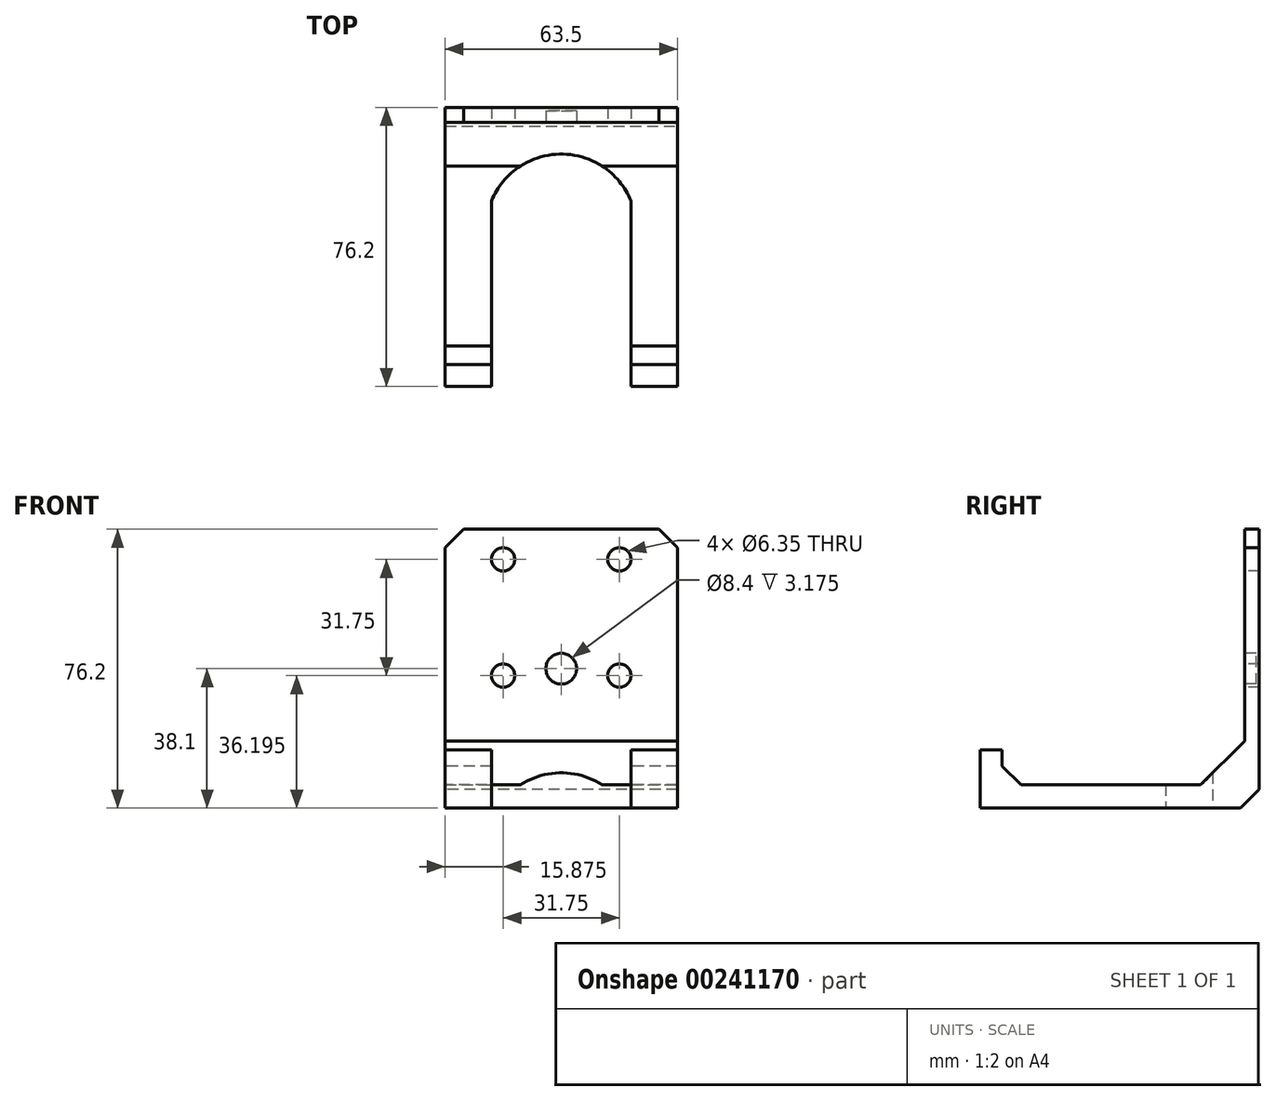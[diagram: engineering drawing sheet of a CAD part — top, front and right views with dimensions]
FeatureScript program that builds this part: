
annotation { "Feature Type Name" : "Feature", "Feature Type Description" : "" }
export const myFeature = defineFeature(function(context is Context, id is Id, definition is map)
    precondition{}
    {
        {
            var Q0;
            Q0=qCreatedBy(makeId("Right.planeOp"),FACE);
            var sketch = newSketch(context, id + "F0", { "sketchPlane" : qUnion([Q0])});
            skLineSegment(sketch, "E0", {"start": v(-72.2, 0) * mm, "end": v(-72.2, 15.87) * mm});
            skLineSegment(sketch, "E1", {"start": v(-72.2, 15.87) * mm, "end": v(-66.2, 15.87) * mm});
            skLineSegment(sketch, "E2", {"start": v(-66.2, 15.87) * mm, "end": v(-66.2, 6.35) * mm});
            skLineSegment(sketch, "E3", {"start": v(-66.2, 6.35) * mm, "end": v(0, 6.35) * mm});
            skLineSegment(sketch, "E4", {"start": v(0, 6.35) * mm, "end": v(0, 76.2) * mm});
            skLineSegment(sketch, "E5", {"start": v(0, 76.2) * mm, "end": v(4, 76.2) * mm});
            skLineSegment(sketch, "E6", {"start": v(4, 76.2) * mm, "end": v(4, 0) * mm});
            skLineSegment(sketch, "E7", {"start": v(4, 0) * mm, "end": v(-72.2, 0) * mm});
            skSolve(sketch);
        }
        {
            var Q0;
            Q0 = qSketchRegion(id + "F0", true);
            extrude(context, id + "F1", {"entities" : qUnion([Q0]), "flatOperationType" : FlatOperationType.REMOVE, "endBound" : BoundingType.SYMMETRIC, "offsetDistance" : 25.4 * mm, "depth" : 63.5 * mm, "domain" : OperationDomain.MODEL});
        }
        {
            var Q0;
            Q0=makeQuery(id+"F1.opExtrude","SWEPT_EDGE",EDGE,{"disambiguationData":[OSD([sQuery(id+"F0.wireOp",EDGE,"E3"),sQuery(id+"F0.wireOp",EDGE,"E4")])]});
            chamfer(context, id + "F2", {"entities" : qUnion([Q0]), "width" : 12 * mm, "tangentPropagation" : true});
        }
        {
            var Q0;
            Q0=qCreatedBy(makeId("Top.planeOp"),FACE);
            var sketch = newSketch(context, id + "F3", { "sketchPlane" : qUnion([Q0])});
            skLineSegment(sketch, "E8", {"start": v(-19.05, -72.2) * mm, "end": v(19.05, -72.2) * mm});
            skLineSegment(sketch, "E9", {"start": v(19.05, -72.2) * mm, "end": v(19.05, -21.52) * mm});
            skLineSegment(sketch, "E10", {"start": v(-19.05, -72.2) * mm, "end": v(-19.05, -21.52) * mm});
            skArc(sketch, "E11", {"start": v(19.05, -21.52) * mm, "mid": v(0, -8.7) * mm, "end": v(-19.05, -21.52) * mm});
            skSolve(sketch);
        }
        {
            var Q0;
            Q0 = qSketchRegion(id + "F3", true);
            extrude(context, id + "F4", {"entities" : qUnion([Q0]), "operationType" : NewBodyOperationType.REMOVE, "depth" : 25.4 * mm});
        }
        {
            var Q0;
            Q0=makeQuery(id+"F1.opExtrude","SWEPT_FACE",FACE,{"disambiguationData":[OSD([sQuery(id+"F0.wireOp",EDGE,"E4")])]});
            var sketch = newSketch(context, id + "F5", { "sketchPlane" : qUnion([Q0])});
            skCircle(sketch, "E12", {"center": v(-15.88, 67.95) * mm, "radius": 3.18 * mm});
            skCircle(sketch, "E13", {"center": v(15.88, 67.95) * mm, "radius": 3.18 * mm});
            skCircle(sketch, "E14", {"center": v(-15.87, 36.2) * mm, "radius": 3.18 * mm});
            skCircle(sketch, "E15", {"center": v(15.88, 36.2) * mm, "radius": 3.18 * mm});
            skSolve(sketch);
        }
        {
            var Q0;
            Q0 = qSketchRegion(id + "F5", true);
            extrude(context, id + "F6", {"entities" : qUnion([Q0]), "operationType" : NewBodyOperationType.REMOVE, "oppositeDirection" : true, "depth" : 25.4 * mm});
        }
        {
            var Q0;
            {var subQ0=sQuery(id+"F0.wireOp",EDGE,"E3");var subQ1=sQuery(id+"F0.wireOp",EDGE,"E2");Q0=makeQuery(id+"F4.boolean.opBoolean","SPLIT",EDGE,{"disambiguationData":[TD([makeQuery(id+"F4.opExtrude","SWEPT_FACE",FACE,{"disambiguationData":[OSD([sQuery(id+"F3.wireOp",EDGE,"E9")])]})])],"derivedFrom":makeQuery(id+"F1.opExtrude","SWEPT_EDGE",EDGE,{"disambiguationData":[OSD([subQ1,subQ0])]})});}
            var Q1;
            {var subQ0=sQuery(id+"F0.wireOp",EDGE,"E3");var subQ1=sQuery(id+"F0.wireOp",EDGE,"E2");Q1=makeQuery(id+"F4.boolean.opBoolean","SPLIT",EDGE,{"disambiguationData":[TD([makeQuery(id+"F4.opExtrude","SWEPT_FACE",FACE,{"disambiguationData":[OSD([sQuery(id+"F3.wireOp",EDGE,"E10")])]})])],"derivedFrom":makeQuery(id+"F1.opExtrude","SWEPT_EDGE",EDGE,{"disambiguationData":[OSD([subQ1,subQ0])]})});}
            chamfer(context, id + "F7", {"entities" : qUnion([Q0, Q1]), "width" : 5.08 * mm, "tangentPropagation" : true});
        }
        {
            var Q0;
            Q0=makeQuery(id+"F1.opExtrude","SWEPT_FACE",FACE,{"disambiguationData":[OSD([sQuery(id+"F0.wireOp",EDGE,"E4")])]});
            var sketch = newSketch(context, id + "F8", { "sketchPlane" : qUnion([Q0])});
            skCircle(sketch, "E16", {"center": v(0, 38.1) * mm, "radius": 4.2 * mm});
            skSolve(sketch);
        }
        {
            var Q0;
            Q0 = qSketchRegion(id + "F8", true);
            extrude(context, id + "F9", {"entities" : qUnion([Q0]), "operationType" : NewBodyOperationType.REMOVE, "oppositeDirection" : true, "depth" : 3.17 * mm, "offsetDistance" : 25.4 * mm});
        }
        {
            var Q0;
            Q0=makeQuery(id+"F1.opExtrude","CAP_EDGE",EDGE,{"disambiguationData":[OSD([sQuery(id+"F0.wireOp",EDGE,"E5")])],"isStart":false});
            var Q1;
            Q1=makeQuery(id+"F1.opExtrude","CAP_EDGE",EDGE,{"disambiguationData":[OSD([sQuery(id+"F0.wireOp",EDGE,"E5")])],"isStart":true});
            var Q2;
            Q2=makeQuery(id+"F1.opExtrude","SWEPT_EDGE",EDGE,{"disambiguationData":[OSD([sQuery(id+"F0.wireOp",EDGE,"E6"),sQuery(id+"F0.wireOp",EDGE,"E7")])]});
            chamfer(context, id + "F10", {"entities" : qUnion([Q0, Q1, Q2]), "width" : 5.08 * mm, "tangentPropagation" : true});
        }
    });
